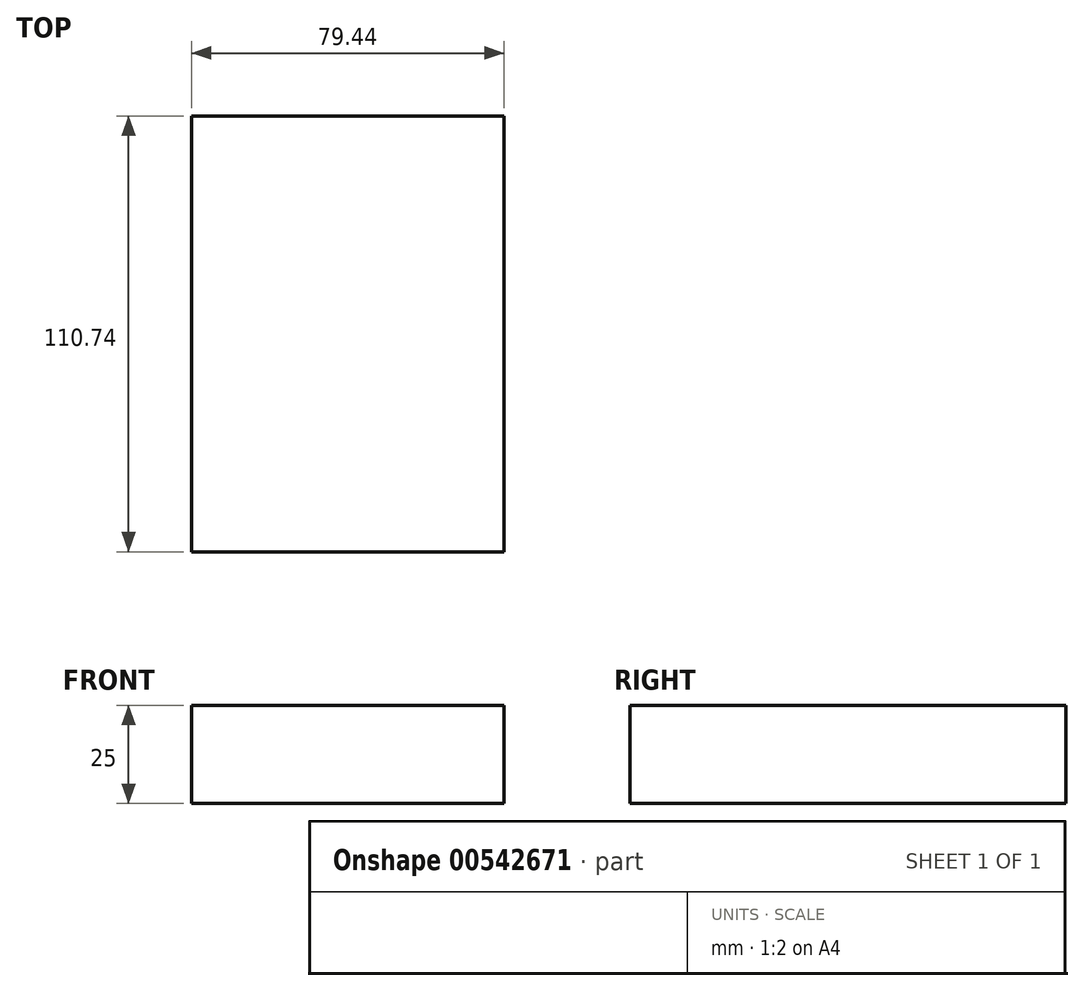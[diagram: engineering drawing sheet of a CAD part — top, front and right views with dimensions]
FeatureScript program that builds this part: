
annotation { "Feature Type Name" : "Feature", "Feature Type Description" : "" }
export const myFeature = defineFeature(function(context is Context, id is Id, definition is map)
    precondition{}
    {
        {
            var Q0;
            Q0=qCreatedBy(makeId("Top.planeOp"),FACE);
            var sketch = newSketch(context, id + "F0", { "sketchPlane" : qUnion([Q0])});
            skLineSegment(sketch, "E0.bottom", {"start": v(-39.72, -55.37) * mm, "end": v(39.72, -55.37) * mm});
            skLineSegment(sketch, "E0.top", {"start": v(-39.72, 55.37) * mm, "end": v(39.72, 55.37) * mm});
            skLineSegment(sketch, "E0.left", {"start": v(-39.72, -55.37) * mm, "end": v(-39.72, 55.37) * mm});
            skLineSegment(sketch, "E0.right", {"start": v(39.72, -55.37) * mm, "end": v(39.72, 55.37) * mm});
            skPoint(sketch, "E0.middle", {"position": v(0, 0) * mm});
            skSolve(sketch);
        }
        {
            var Q0;
            Q0=makeQuery(id+"F0.imprint","IMPRINT",FACE,{"disambiguationData":[TD([[makeQuery(id+"F0.imprint","IMPRINT",EDGE,{"derivedFrom":sQuery(id+"F0.wireOp",EDGE,"E0.bottom")}),1.0]])]});
            extrude(context, id + "F1", {"entities" : qUnion([Q0]), "depth" : 25 * mm, "offsetDistance" : 25.4 * mm});
        }
        {
            var Q0;
            Q0=makeQuery(id+"F1.opExtrude","CAP_FACE",FACE,{"disambiguationData":[OSD([sQuery(id+"F0.wireOp",EDGE,"E0.bottom"),sQuery(id+"F0.wireOp",EDGE,"E0.top"),sQuery(id+"F0.wireOp",EDGE,"E0.left"),sQuery(id+"F0.wireOp",EDGE,"E0.right")])],"isStart":false});
            var sketch = newSketch(context, id + "F2", { "sketchPlane" : qUnion([Q0])});
            skCircle(sketch, "E1", {"center": v(0, 0) * mm, "radius": 3.75 * mm});
            skCircle(sketch, "E2", {"center": v(0, 0) * mm, "radius": 14.58 * mm});
            skSolve(sketch);
        }
        {
            var Q0;
            Q0 = qSketchRegion(id + "F2", true);
            extrude(context, id + "F3", {"entities" : qUnion([Q0]), "operationType" : NewBodyOperationType.ADD, "oppositeDirection" : true, "depth" : 25 * mm, "offsetDistance" : 25.4 * mm});
        }
    });
